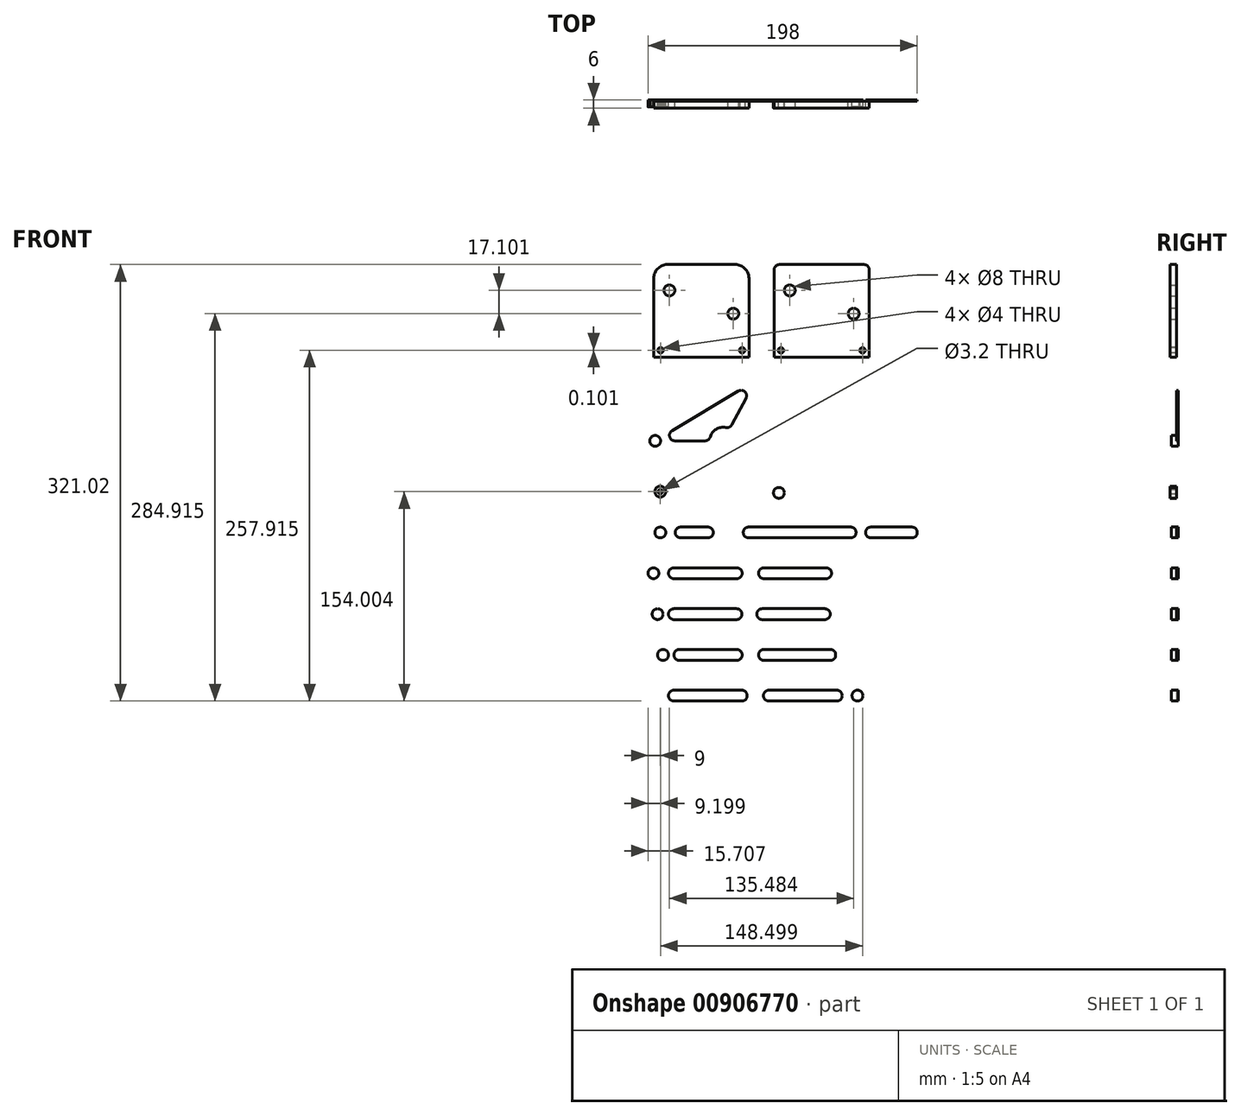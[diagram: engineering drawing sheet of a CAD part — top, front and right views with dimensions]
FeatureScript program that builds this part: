
annotation { "Feature Type Name" : "Feature", "Feature Type Description" : "" }
export const myFeature = defineFeature(function(context is Context, id is Id, definition is map)
    precondition{}
    {
        {
            var Q0;
            Q0=qCreatedBy(makeId("Front.planeOp"),FACE);
            var sketch = newSketch(context, id + "F0", { "sketchPlane" : qUnion([Q0])});
            skCircle(sketch, "E0", {"center": v(-102.5, -60.26) * mm, "radius": 4 * mm});
            skCircle(sketch, "E1", {"center": v(39.5, -60.26) * mm, "radius": 4 * mm});
            skCircle(sketch, "E2", {"center": v(-101.24, 37.12) * mm, "radius": 4 * mm});
            skCircle(sketch, "E3", {"center": v(-51.24, 37.12) * mm, "radius": 4 * mm});
            skCircle(sketch, "E4", {"center": v(-97.5, -30.26) * mm, "radius": 4 * mm});
            skCircle(sketch, "E5", {"center": v(47.5, -150.26) * mm, "radius": 4 * mm});
            skCircle(sketch, "E6", {"center": v(-102.5, -150.26) * mm, "radius": 4 * mm});
            skCircle(sketch, "E7", {"center": v(-97.5, -0.26) * mm, "radius": 4 * mm});
            skCircle(sketch, "E8", {"center": v(-47.5, -0.26) * mm, "radius": 4 * mm});
            skArc(sketch, "E9", {"start": v(-102.5, -142.76) * mm, "mid": v(-110, -150.26) * mm, "end": v(-102.5, -157.76) * mm});
            skArc(sketch, "E10", {"start": v(47.5, -157.76) * mm, "mid": v(55, -150.26) * mm, "end": v(47.5, -142.76) * mm});
            skLineSegment(sketch, "E11", {"start": v(47.5, -142.76) * mm, "end": v(-102.5, -142.76) * mm});
            skLineSegment(sketch, "E12", {"start": v(47.5, -157.76) * mm, "end": v(-102.5, -157.76) * mm});
            skArc(sketch, "E13", {"start": v(-87.5, -146.26) * mm, "mid": v(-91.5, -150.26) * mm, "end": v(-87.5, -154.26) * mm});
            skArc(sketch, "E14", {"start": v(-37.62, -154.26) * mm, "mid": v(-33.62, -150.26) * mm, "end": v(-37.62, -146.26) * mm});
            skLineSegment(sketch, "E15", {"start": v(-87.5, -146.26) * mm, "end": v(-37.62, -146.26) * mm});
            skLineSegment(sketch, "E16", {"start": v(-87.5, -154.26) * mm, "end": v(-37.62, -154.26) * mm});
            skLineSegment(sketch, "E17", {"start": v(32.27, -146.26) * mm, "end": v(-17.62, -146.26) * mm});
            skLineSegment(sketch, "E18", {"start": v(32.27, -154.26) * mm, "end": v(-17.62, -154.26) * mm});
            skArc(sketch, "E19", {"start": v(32.27, -154.26) * mm, "mid": v(36.27, -150.26) * mm, "end": v(32.27, -146.26) * mm});
            skArc(sketch, "E20", {"start": v(-17.62, -146.26) * mm, "mid": v(-21.62, -150.26) * mm, "end": v(-17.62, -154.26) * mm});
            skArc(sketch, "E21", {"start": v(-102.5, -52.76) * mm, "mid": v(-110, -60.26) * mm, "end": v(-102.5, -67.76) * mm});
            skArc(sketch, "E22", {"start": v(39.5, -67.76) * mm, "mid": v(47, -60.26) * mm, "end": v(39.5, -52.76) * mm});
            skLineSegment(sketch, "E23", {"start": v(-102.5, -52.76) * mm, "end": v(39.5, -52.76) * mm});
            skLineSegment(sketch, "E24", {"start": v(39.5, -52.76) * mm, "end": v(-8.11, -52.76) * mm});
            skLineSegment(sketch, "E25", {"start": v(-102.5, -67.76) * mm, "end": v(39.5, -67.76) * mm});
            skArc(sketch, "E26", {"start": v(-87.5, -56.26) * mm, "mid": v(-91.5, -60.26) * mm, "end": v(-87.5, -64.26) * mm});
            skArc(sketch, "E27", {"start": v(-41.27, -64.26) * mm, "mid": v(-37.27, -60.26) * mm, "end": v(-41.27, -56.26) * mm});
            skLineSegment(sketch, "E28", {"start": v(-87.5, -56.26) * mm, "end": v(-41.27, -56.26) * mm});
            skLineSegment(sketch, "E29", {"start": v(-87.5, -64.26) * mm, "end": v(-41.27, -64.26) * mm});
            skLineSegment(sketch, "E30", {"start": v(24.5, -56.26) * mm, "end": v(-21.27, -56.26) * mm});
            skLineSegment(sketch, "E31", {"start": v(24.5, -64.26) * mm, "end": v(-21.27, -64.26) * mm});
            skArc(sketch, "E32", {"start": v(-21.27, -56.26) * mm, "mid": v(-25.27, -60.26) * mm, "end": v(-21.27, -64.26) * mm});
            skArc(sketch, "E33", {"start": v(-97.5, 7.24) * mm, "mid": v(-105, -0.26) * mm, "end": v(-97.5, -7.76) * mm});
            skArc(sketch, "E34", {"start": v(-47.5, -7.76) * mm, "mid": v(-40, -0.26) * mm, "end": v(-47.5, 7.24) * mm});
            skLineSegment(sketch, "E35", {"start": v(-97.5, 7.24) * mm, "end": v(-47.5, 7.24) * mm});
            skLineSegment(sketch, "E36", {"start": v(-97.5, -7.76) * mm, "end": v(-47.5, -7.76) * mm});
            skCircle(sketch, "E37", {"center": v(-10.28, -1.13) * mm, "radius": 4 * mm});
            skCircle(sketch, "E38", {"center": v(39.72, -1.13) * mm, "radius": 4 * mm});
            skLineSegment(sketch, "E39", {"start": v(-10.28, 6.37) * mm, "end": v(39.72, 6.37) * mm});
            skLineSegment(sketch, "E40", {"start": v(39.72, -8.63) * mm, "end": v(-10.28, -8.63) * mm});
            skArc(sketch, "E41", {"start": v(-10.28, 6.37) * mm, "mid": v(-17.78, -1.13) * mm, "end": v(-10.28, -8.63) * mm});
            skArc(sketch, "E42", {"start": v(39.72, -8.63) * mm, "mid": v(47.22, -1.13) * mm, "end": v(39.72, 6.37) * mm});
            skArc(sketch, "E43", {"start": v(24.5, -64.26) * mm, "mid": v(28.5, -60.26) * mm, "end": v(24.5, -56.26) * mm});
            skCircle(sketch, "E44", {"center": v(-99.5, -90.32) * mm, "radius": 4 * mm});
            skCircle(sketch, "E45", {"center": v(35.5, -90.32) * mm, "radius": 4 * mm});
            skArc(sketch, "E46", {"start": v(-87.5, -86.32) * mm, "mid": v(-91.5, -90.32) * mm, "end": v(-87.5, -94.32) * mm});
            skArc(sketch, "E47", {"start": v(-41.5, -94.32) * mm, "mid": v(-37.5, -90.32) * mm, "end": v(-41.5, -86.32) * mm});
            skLineSegment(sketch, "E48", {"start": v(-87.5, -86.32) * mm, "end": v(-41.27, -86.32) * mm});
            skLineSegment(sketch, "E49", {"start": v(-87.5, -94.32) * mm, "end": v(-41.27, -94.32) * mm});
            skArc(sketch, "E50", {"start": v(-22.5, -86.32) * mm, "mid": v(-26.5, -90.32) * mm, "end": v(-22.5, -94.32) * mm});
            skLineSegment(sketch, "E51", {"start": v(35.5, -82.82) * mm, "end": v(-8.11, -82.82) * mm});
            skLineSegment(sketch, "E52", {"start": v(-99.5, -97.82) * mm, "end": v(35.5, -97.82) * mm});
            skLineSegment(sketch, "E53", {"start": v(-99.5, -82.82) * mm, "end": v(35.5, -82.82) * mm});
            skArc(sketch, "E54", {"start": v(23.5, -94.32) * mm, "mid": v(27.5, -90.32) * mm, "end": v(23.5, -86.32) * mm});
            skLineSegment(sketch, "E55", {"start": v(24.5, -86.32) * mm, "end": v(-22.5, -86.32) * mm});
            skLineSegment(sketch, "E56", {"start": v(24.5, -94.32) * mm, "end": v(-22.5, -94.32) * mm});
            skCircle(sketch, "E57", {"center": v(-95.5, -120.32) * mm, "radius": 4 * mm});
            skCircle(sketch, "E58", {"center": v(39.5, -120.32) * mm, "radius": 4 * mm});
            skArc(sketch, "E59", {"start": v(39.5, -127.82) * mm, "mid": v(47, -120.32) * mm, "end": v(39.5, -112.82) * mm});
            skArc(sketch, "E60", {"start": v(-83.5, -116.32) * mm, "mid": v(-87.5, -120.32) * mm, "end": v(-83.5, -124.32) * mm});
            skArc(sketch, "E61", {"start": v(-41.27, -124.32) * mm, "mid": v(-37.27, -120.32) * mm, "end": v(-41.27, -116.32) * mm});
            skLineSegment(sketch, "E62", {"start": v(-83.5, -116.32) * mm, "end": v(-39.27, -116.32) * mm});
            skLineSegment(sketch, "E63", {"start": v(-83.5, -124.32) * mm, "end": v(-39.27, -124.32) * mm});
            skArc(sketch, "E64", {"start": v(-21.27, -116.32) * mm, "mid": v(-25.27, -120.32) * mm, "end": v(-21.27, -124.32) * mm});
            skLineSegment(sketch, "E65", {"start": v(39.5, -112.82) * mm, "end": v(-8.11, -112.82) * mm});
            skLineSegment(sketch, "E66", {"start": v(-95.5, -127.82) * mm, "end": v(39.5, -127.82) * mm});
            skLineSegment(sketch, "E67", {"start": v(-95.5, -112.82) * mm, "end": v(39.5, -112.82) * mm});
            skArc(sketch, "E68", {"start": v(27.5, -124.32) * mm, "mid": v(31.5, -120.32) * mm, "end": v(27.5, -116.32) * mm});
            skLineSegment(sketch, "E69", {"start": v(27.5, -116.32) * mm, "end": v(-21.27, -116.32) * mm});
            skLineSegment(sketch, "E70", {"start": v(27.5, -124.32) * mm, "end": v(-21.27, -124.32) * mm});
            skCircle(sketch, "E71", {"center": v(-47.5, -30.26) * mm, "radius": 4 * mm});
            skArc(sketch, "E72", {"start": v(-97.5, -22.76) * mm, "mid": v(-105, -30.26) * mm, "end": v(-97.5, -37.76) * mm});
            skLineSegment(sketch, "E73", {"start": v(-97.5, -22.76) * mm, "end": v(102.5, -22.76) * mm});
            skLineSegment(sketch, "E74", {"start": v(102.5, -37.76) * mm, "end": v(-97.5, -37.76) * mm});
            skArc(sketch, "E75", {"start": v(-82.5, -26.26) * mm, "mid": v(-86.5, -30.26) * mm, "end": v(-82.5, -34.26) * mm});
            skArc(sketch, "E76", {"start": v(-62.5, -34.26) * mm, "mid": v(-58.5, -30.26) * mm, "end": v(-62.5, -26.26) * mm});
            skArc(sketch, "E77", {"start": v(-32.5, -26.26) * mm, "mid": v(-36.5, -30.26) * mm, "end": v(-32.5, -34.26) * mm});
            skArc(sketch, "E78", {"start": v(87.5, -34.26) * mm, "mid": v(91.5, -30.26) * mm, "end": v(87.5, -26.26) * mm});
            skLineSegment(sketch, "E79", {"start": v(-82.5, -26.26) * mm, "end": v(-62.5, -26.26) * mm});
            skLineSegment(sketch, "E80", {"start": v(-62.5, -34.26) * mm, "end": v(-82.5, -34.26) * mm});
            skArc(sketch, "E81", {"start": v(42.5, -34.26) * mm, "mid": v(46.5, -30.26) * mm, "end": v(42.5, -26.26) * mm});
            skArc(sketch, "E82", {"start": v(57.5, -26.26) * mm, "mid": v(53.5, -30.26) * mm, "end": v(57.5, -34.26) * mm});
            skLineSegment(sketch, "E83", {"start": v(-32.5, -26.26) * mm, "end": v(42.5, -26.26) * mm});
            skLineSegment(sketch, "E84", {"start": v(57.5, -26.26) * mm, "end": v(87.5, -26.26) * mm});
            skLineSegment(sketch, "E85", {"start": v(57.5, -34.26) * mm, "end": v(87.5, -34.26) * mm});
            skLineSegment(sketch, "E86", {"start": v(-32.5, -34.26) * mm, "end": v(42.5, -34.26) * mm});
            skCircle(sketch, "E87", {"center": v(102.5, -30.26) * mm, "radius": 4 * mm});
            skArc(sketch, "E88", {"start": v(102.5, -37.76) * mm, "mid": v(110, -30.26) * mm, "end": v(102.5, -22.76) * mm});
            skCircle(sketch, "E89", {"center": v(14.72, -1.07) * mm, "radius": 3.25 * mm});
            skCircle(sketch, "E90", {"center": v(-27.7, 81.17) * mm, "radius": 4 * mm});
            skArc(sketch, "E91", {"start": v(-105.1, 43.55) * mm, "mid": v(-108.47, 35.12) * mm, "end": v(-101.24, 29.62) * mm});
            skArc(sketch, "E92", {"start": v(-51.24, 29.62) * mm, "mid": v(-47.39, 30.68) * mm, "end": v(-44.63, 33.58) * mm});
            skArc(sketch, "E93", {"start": v(-21.09, 77.63) * mm, "mid": v(-22.53, 86.6) * mm, "end": v(-31.56, 87.6) * mm});
            skLineSegment(sketch, "E94", {"start": v(-86.78, 37.12) * mm, "end": v(-64.66, 37.12) * mm});
            skLineSegment(sketch, "E95", {"start": v(-44.92, 48.95) * mm, "end": v(-34.51, 68.43) * mm});
            skLineSegment(sketch, "E96", {"start": v(-40.1, 73.75) * mm, "end": v(-88.84, 44.55) * mm});
            skLineSegment(sketch, "E97", {"start": v(-31.56, 87.6) * mm, "end": v(-105.1, 43.55) * mm});
            skLineSegment(sketch, "E98", {"start": v(-44.63, 33.58) * mm, "end": v(-21.09, 77.63) * mm});
            skLineSegment(sketch, "E99", {"start": v(-101.24, 29.62) * mm, "end": v(-51.24, 29.62) * mm});
            skArc(sketch, "E100", {"start": v(-88.84, 44.55) * mm, "mid": v(-90.64, 40.05) * mm, "end": v(-86.78, 37.12) * mm});
            skArc(sketch, "E101", {"start": v(-34.51, 68.43) * mm, "mid": v(-35.28, 73.21) * mm, "end": v(-40.1, 73.75) * mm});
            skArc(sketch, "E102", {"start": v(-49.25, 46.92) * mm, "mid": v(-56.38, 45.7) * mm, "end": v(-60.83, 39.97) * mm});
            skArc(sketch, "E103", {"start": v(-49.25, 46.92) * mm, "mid": v(-46.75, 47.21) * mm, "end": v(-44.92, 48.95) * mm});
            skArc(sketch, "E104", {"start": v(-64.66, 37.12) * mm, "mid": v(-62.27, 37.9) * mm, "end": v(-60.83, 39.97) * mm});
            skLineSegment(sketch, "E105", {"start": v(-102.3, 98.76) * mm, "end": v(-32.3, 98.76) * mm});
            skLineSegment(sketch, "E106", {"start": v(-102.3, 166.76) * mm, "end": v(-102.3, 98.65) * mm});
            skLineSegment(sketch, "E107", {"start": v(-32.3, 98.65) * mm, "end": v(-32.3, 166.76) * mm});
            skCircle(sketch, "E108", {"center": v(-90.8, 147.76) * mm, "radius": 4 * mm});
            skCircle(sketch, "E109", {"center": v(-43.8, 130.65) * mm, "radius": 4 * mm});
            skLineSegment(sketch, "E110", {"start": v(-13.8, 98.65) * mm, "end": v(56.2, 98.65) * mm});
            skLineSegment(sketch, "E111", {"start": v(-9.8, 166.76) * mm, "end": v(52.2, 166.76) * mm});
            skLineSegment(sketch, "E112", {"start": v(-13.8, 162.76) * mm, "end": v(-13.8, 98.65) * mm});
            skLineSegment(sketch, "E113", {"start": v(56.2, 98.65) * mm, "end": v(56.2, 162.76) * mm});
            skCircle(sketch, "E114", {"center": v(-2.3, 147.76) * mm, "radius": 4 * mm});
            skCircle(sketch, "E115", {"center": v(44.7, 130.65) * mm, "radius": 4 * mm});
            skArc(sketch, "E116", {"start": v(56.2, 162.76) * mm, "mid": v(55.03, 165.58) * mm, "end": v(52.2, 166.76) * mm});
            skArc(sketch, "E117", {"start": v(-9.8, 166.76) * mm, "mid": v(-12.63, 165.58) * mm, "end": v(-13.8, 162.76) * mm});
            skCircle(sketch, "E118", {"center": v(-97.5, -0.26) * mm, "radius": 1.6 * mm});
            skCircle(sketch, "E119", {"center": v(-47.5, -0.26) * mm, "radius": 1.6 * mm});
            skArc(sketch, "E120", {"start": v(-95.5, -112.82) * mm, "mid": v(-103, -120.32) * mm, "end": v(-95.5, -127.82) * mm});
            skArc(sketch, "E121", {"start": v(35.5, -97.82) * mm, "mid": v(43, -90.32) * mm, "end": v(35.5, -82.82) * mm});
            skArc(sketch, "E122", {"start": v(-99.5, -82.82) * mm, "mid": v(-107, -90.32) * mm, "end": v(-99.5, -97.82) * mm});
            skLineSegment(sketch, "E123.0", {"start": v(-102.3, 166.76) * mm, "end": v(-32.3, 166.76) * mm});
            skSolve(sketch);
        }
        {
            var Q0;
            Q0=makeQuery(id+"F0.imprint","IMPRINT",FACE,{"disambiguationData":[TD([[makeQuery(id+"F0.imprint","IMPRINT",EDGE,{"derivedFrom":sQuery(id+"F0.wireOp",EDGE,"E105")}),1.0]])]});
            extrude(context, id + "F1", {"entities" : qUnion([Q0]), "depth" : 5 * mm, "offsetDistance" : 25 * mm});
        }
        {
            var Q0;
            Q0=makeQuery(id+"F0.imprint","IMPRINT",FACE,{"disambiguationData":[TD([[makeQuery(id+"F0.imprint","IMPRINT",EDGE,{"derivedFrom":sQuery(id+"F0.wireOp",EDGE,"E2")}),1.0]])]});
            extrude(context, id + "F2", {"entities" : qUnion([Q0]), "depth" : 4 * mm, "offsetDistance" : 25 * mm});
        }
        {
            var Q0;
            Q0=makeQuery(id+"F0.imprint","IMPRINT",FACE,{"disambiguationData":[TD([[makeQuery(id+"F0.imprint","IMPRINT",EDGE,{"derivedFrom":sQuery(id+"F0.wireOp",EDGE,"E94")}),1.0]])]});
            var Q1;
            Q1=makeQuery(id+"F0.imprint","IMPRINT",FACE,{"disambiguationData":[TD([[makeQuery(id+"F0.imprint","IMPRINT",EDGE,{"derivedFrom":sQuery(id+"F0.wireOp",EDGE,"E2")}),1.0]])]});
            extrude(context, id + "F3", {"entities" : qUnion([Q0, Q1]), "operationType" : NewBodyOperationType.ADD, "oppositeDirection" : true, "depth" : 1 * mm, "offsetDistance" : 25 * mm});
        }
        {
            var Q0;
            Q0=makeQuery(id+"F0.imprint","IMPRINT",FACE,{"disambiguationData":[TD([[makeQuery(id+"F0.imprint","IMPRINT",EDGE,{"derivedFrom":sQuery(id+"F0.wireOp",EDGE,"E4")}),1.0]])]});
            extrude(context, id + "F4", {"entities" : qUnion([Q0]), "depth" : 4 * mm, "offsetDistance" : 25 * mm});
        }
        {
            var Q0;
            Q0=makeQuery(id+"F4.opExtrude","CAP_FACE",FACE,{"disambiguationData":[OSD([sQuery(id+"F0.wireOp",EDGE,"E4"),sQuery(id+"F0.wireOp",EDGE,"E71"),sQuery(id+"F0.wireOp",EDGE,"E72"),sQuery(id+"F0.wireOp",EDGE,"E73"),sQuery(id+"F0.wireOp",EDGE,"E74"),sQuery(id+"F0.wireOp",EDGE,"E75"),sQuery(id+"F0.wireOp",EDGE,"E76"),sQuery(id+"F0.wireOp",EDGE,"E77"),sQuery(id+"F0.wireOp",EDGE,"E78"),sQuery(id+"F0.wireOp",EDGE,"E79"),sQuery(id+"F0.wireOp",EDGE,"E80"),sQuery(id+"F0.wireOp",EDGE,"E81"),sQuery(id+"F0.wireOp",EDGE,"E82"),sQuery(id+"F0.wireOp",EDGE,"E83"),sQuery(id+"F0.wireOp",EDGE,"E84"),sQuery(id+"F0.wireOp",EDGE,"E85"),sQuery(id+"F0.wireOp",EDGE,"E86"),sQuery(id+"F0.wireOp",EDGE,"E87"),sQuery(id+"F0.wireOp",EDGE,"E88")])],"isStart":false});
            var Q1;
            Q1=makeQuery(id+"F0.imprint","IMPRINT",FACE,{"disambiguationData":[TD([[makeQuery(id+"F0.imprint","IMPRINT",EDGE,{"derivedFrom":sQuery(id+"F0.wireOp",EDGE,"E75")}),1.0]])]});
            var Q2;
            Q2=makeQuery(id+"F0.imprint","IMPRINT",FACE,{"disambiguationData":[TD([[makeQuery(id+"F0.imprint","IMPRINT",EDGE,{"derivedFrom":sQuery(id+"F0.wireOp",EDGE,"E77")}),1.0]])]});
            var Q3;
            Q3=makeQuery(id+"F0.imprint","IMPRINT",FACE,{"disambiguationData":[TD([[makeQuery(id+"F0.imprint","IMPRINT",EDGE,{"derivedFrom":sQuery(id+"F0.wireOp",EDGE,"E78")}),1.0]])]});
            extrude(context, id + "F5", {"entities" : qUnion([Q0, Q1, Q2, Q3]), "operationType" : NewBodyOperationType.ADD, "oppositeDirection" : true, "depth" : 1 * mm, "offsetDistance" : 25 * mm});
        }
        {
            var Q0;
            Q0=makeQuery(id+"F0.imprint","IMPRINT",FACE,{"disambiguationData":[TD([[makeQuery(id+"F0.imprint","IMPRINT",EDGE,{"derivedFrom":sQuery(id+"F0.wireOp",EDGE,"E4")}),1.0]])]});
            var Q1;
            Q1=makeQuery(id+"F0.imprint","IMPRINT",FACE,{"disambiguationData":[TD([[makeQuery(id+"F0.imprint","IMPRINT",EDGE,{"derivedFrom":sQuery(id+"F0.wireOp",EDGE,"E87")}),-1.0]])]});
            var Q2;
            Q2=makeQuery(id+"F0.imprint","IMPRINT",FACE,{"disambiguationData":[TD([[makeQuery(id+"F0.imprint","IMPRINT",EDGE,{"derivedFrom":sQuery(id+"F0.wireOp",EDGE,"E78")}),1.0]])]});
            var Q3;
            Q3=makeQuery(id+"F0.imprint","IMPRINT",FACE,{"disambiguationData":[TD([[makeQuery(id+"F0.imprint","IMPRINT",EDGE,{"derivedFrom":sQuery(id+"F0.wireOp",EDGE,"E77")}),1.0]])]});
            var Q4;
            Q4=makeQuery(id+"F0.imprint","IMPRINT",FACE,{"disambiguationData":[TD([[makeQuery(id+"F0.imprint","IMPRINT",EDGE,{"derivedFrom":sQuery(id+"F0.wireOp",EDGE,"E71")}),-1.0]])]});
            var Q5;
            Q5=makeQuery(id+"F0.imprint","IMPRINT",FACE,{"disambiguationData":[TD([[makeQuery(id+"F0.imprint","IMPRINT",EDGE,{"derivedFrom":sQuery(id+"F0.wireOp",EDGE,"E75")}),1.0]])]});
            var Q6;
            Q6=makeQuery(id+"F0.imprint","IMPRINT",FACE,{"disambiguationData":[TD([[makeQuery(id+"F0.imprint","IMPRINT",EDGE,{"derivedFrom":sQuery(id+"F0.wireOp",EDGE,"E4")}),-1.0]])]});
            extrude(context, id + "F6", {"entities" : qUnion([Q0, Q1, Q2, Q3, Q4, Q5, Q6]), "operationType" : NewBodyOperationType.ADD, "oppositeDirection" : true, "depth" : 1 * mm, "offsetDistance" : 25 * mm});
        }
        {
            var Q0;
            Q0=makeQuery(id+"F0.imprint","IMPRINT",FACE,{"disambiguationData":[TD([[makeQuery(id+"F0.imprint","IMPRINT",EDGE,{"derivedFrom":sQuery(id+"F0.wireOp",EDGE,"E0")}),1.0]])]});
            extrude(context, id + "F7", {"entities" : qUnion([Q0]), "depth" : 4 * mm, "offsetDistance" : 25 * mm});
        }
        {
            var Q0;
            Q0=makeQuery(id+"F0.imprint","IMPRINT",FACE,{"disambiguationData":[TD([[makeQuery(id+"F0.imprint","IMPRINT",EDGE,{"derivedFrom":sQuery(id+"F0.wireOp",EDGE,"E0")}),1.0]])]});
            var Q1;
            Q1=makeQuery(id+"F0.imprint","IMPRINT",FACE,{"disambiguationData":[TD([[makeQuery(id+"F0.imprint","IMPRINT",EDGE,{"derivedFrom":sQuery(id+"F0.wireOp",EDGE,"E1")}),-1.0]])]});
            var Q2;
            Q2=makeQuery(id+"F0.imprint","IMPRINT",FACE,{"disambiguationData":[TD([[makeQuery(id+"F0.imprint","IMPRINT",EDGE,{"derivedFrom":sQuery(id+"F0.wireOp",EDGE,"E30")}),1.0]])]});
            var Q3;
            Q3=makeQuery(id+"F0.imprint","IMPRINT",FACE,{"disambiguationData":[TD([[makeQuery(id+"F0.imprint","IMPRINT",EDGE,{"derivedFrom":sQuery(id+"F0.wireOp",EDGE,"E26")}),1.0]])]});
            var Q4;
            Q4=makeQuery(id+"F0.imprint","IMPRINT",FACE,{"disambiguationData":[TD([[makeQuery(id+"F0.imprint","IMPRINT",EDGE,{"derivedFrom":sQuery(id+"F0.wireOp",EDGE,"E0")}),-1.0]])]});
            extrude(context, id + "F8", {"entities" : qUnion([Q0, Q1, Q2, Q3, Q4]), "operationType" : NewBodyOperationType.ADD, "oppositeDirection" : true, "depth" : 1 * mm, "offsetDistance" : 25 * mm});
        }
        {
            var Q0;
            Q0=makeQuery(id+"F0.imprint","IMPRINT",FACE,{"disambiguationData":[TD([[makeQuery(id+"F0.imprint","IMPRINT",EDGE,{"derivedFrom":sQuery(id+"F0.wireOp",EDGE,"E44")}),1.0]])]});
            extrude(context, id + "F9", {"entities" : qUnion([Q0]), "depth" : 4 * mm, "offsetDistance" : 25 * mm});
        }
        {
            var Q0;
            Q0=makeQuery(id+"F0.imprint","IMPRINT",FACE,{"disambiguationData":[TD([[makeQuery(id+"F0.imprint","IMPRINT",EDGE,{"derivedFrom":sQuery(id+"F0.wireOp",EDGE,"E44")}),1.0]])]});
            var Q1;
            Q1=makeQuery(id+"F0.imprint","IMPRINT",FACE,{"disambiguationData":[TD([[makeQuery(id+"F0.imprint","IMPRINT",EDGE,{"derivedFrom":sQuery(id+"F0.wireOp",EDGE,"E45")}),-1.0]])]});
            var Q2;
            Q2=makeQuery(id+"F0.imprint","IMPRINT",FACE,{"disambiguationData":[TD([[makeQuery(id+"F0.imprint","IMPRINT",EDGE,{"derivedFrom":sQuery(id+"F0.wireOp",EDGE,"E50")}),1.0]])]});
            var Q3;
            Q3=makeQuery(id+"F0.imprint","IMPRINT",FACE,{"disambiguationData":[TD([[makeQuery(id+"F0.imprint","IMPRINT",EDGE,{"derivedFrom":sQuery(id+"F0.wireOp",EDGE,"E46")}),1.0]])]});
            var Q4;
            Q4=makeQuery(id+"F0.imprint","IMPRINT",FACE,{"disambiguationData":[TD([[makeQuery(id+"F0.imprint","IMPRINT",EDGE,{"derivedFrom":sQuery(id+"F0.wireOp",EDGE,"E44")}),-1.0]])]});
            extrude(context, id + "F10", {"entities" : qUnion([Q0, Q1, Q2, Q3, Q4]), "operationType" : NewBodyOperationType.ADD, "oppositeDirection" : true, "depth" : 1 * mm, "offsetDistance" : 25 * mm});
        }
        {
            var Q0;
            Q0=makeQuery(id+"F0.imprint","IMPRINT",FACE,{"disambiguationData":[TD([[makeQuery(id+"F0.imprint","IMPRINT",EDGE,{"derivedFrom":sQuery(id+"F0.wireOp",EDGE,"E57")}),1.0]])]});
            extrude(context, id + "F11", {"entities" : qUnion([Q0]), "depth" : 4 * mm, "offsetDistance" : 25 * mm});
        }
        {
            var Q0;
            Q0=makeQuery(id+"F0.imprint","IMPRINT",FACE,{"disambiguationData":[TD([[makeQuery(id+"F0.imprint","IMPRINT",EDGE,{"derivedFrom":sQuery(id+"F0.wireOp",EDGE,"E57")}),1.0]])]});
            var Q1;
            Q1=makeQuery(id+"F0.imprint","IMPRINT",FACE,{"disambiguationData":[TD([[makeQuery(id+"F0.imprint","IMPRINT",EDGE,{"derivedFrom":sQuery(id+"F0.wireOp",EDGE,"E58")}),-1.0]])]});
            var Q2;
            Q2=makeQuery(id+"F0.imprint","IMPRINT",FACE,{"disambiguationData":[TD([[makeQuery(id+"F0.imprint","IMPRINT",EDGE,{"derivedFrom":sQuery(id+"F0.wireOp",EDGE,"E64")}),1.0]])]});
            var Q3;
            Q3=makeQuery(id+"F0.imprint","IMPRINT",FACE,{"disambiguationData":[TD([[makeQuery(id+"F0.imprint","IMPRINT",EDGE,{"derivedFrom":sQuery(id+"F0.wireOp",EDGE,"E60")}),1.0]])]});
            var Q4;
            Q4=makeQuery(id+"F0.imprint","IMPRINT",FACE,{"disambiguationData":[TD([[makeQuery(id+"F0.imprint","IMPRINT",EDGE,{"derivedFrom":sQuery(id+"F0.wireOp",EDGE,"E57")}),-1.0]])]});
            extrude(context, id + "F12", {"entities" : qUnion([Q0, Q1, Q2, Q3, Q4]), "operationType" : NewBodyOperationType.ADD, "oppositeDirection" : true, "depth" : 1 * mm, "offsetDistance" : 25 * mm});
        }
        {
            var Q0;
            Q0=makeQuery(id+"F0.imprint","IMPRINT",FACE,{"disambiguationData":[TD([[makeQuery(id+"F0.imprint","IMPRINT",EDGE,{"derivedFrom":sQuery(id+"F0.wireOp",EDGE,"E5")}),1.0]])]});
            extrude(context, id + "F13", {"entities" : qUnion([Q0]), "depth" : 4 * mm, "offsetDistance" : 25 * mm});
        }
        {
            var Q0;
            Q0=makeQuery(id+"F0.imprint","IMPRINT",FACE,{"disambiguationData":[TD([[makeQuery(id+"F0.imprint","IMPRINT",EDGE,{"derivedFrom":sQuery(id+"F0.wireOp",EDGE,"E5")}),1.0]])]});
            var Q1;
            Q1=makeQuery(id+"F0.imprint","IMPRINT",FACE,{"disambiguationData":[TD([[makeQuery(id+"F0.imprint","IMPRINT",EDGE,{"derivedFrom":sQuery(id+"F0.wireOp",EDGE,"E5")}),-1.0]])]});
            var Q2;
            Q2=makeQuery(id+"F0.imprint","IMPRINT",FACE,{"disambiguationData":[TD([[makeQuery(id+"F0.imprint","IMPRINT",EDGE,{"derivedFrom":sQuery(id+"F0.wireOp",EDGE,"E17")}),1.0]])]});
            var Q3;
            Q3=makeQuery(id+"F0.imprint","IMPRINT",FACE,{"disambiguationData":[TD([[makeQuery(id+"F0.imprint","IMPRINT",EDGE,{"derivedFrom":sQuery(id+"F0.wireOp",EDGE,"E13")}),1.0]])]});
            var Q4;
            Q4=makeQuery(id+"F0.imprint","IMPRINT",FACE,{"disambiguationData":[TD([[makeQuery(id+"F0.imprint","IMPRINT",EDGE,{"derivedFrom":sQuery(id+"F0.wireOp",EDGE,"E6")}),-1.0]])]});
            extrude(context, id + "F14", {"entities" : qUnion([Q0, Q1, Q2, Q3, Q4]), "operationType" : NewBodyOperationType.ADD, "oppositeDirection" : true, "depth" : 1 * mm, "offsetDistance" : 25 * mm});
        }
        {
            var Q0;
            Q0=makeQuery(id+"F0.imprint","IMPRINT",FACE,{"disambiguationData":[TD([[makeQuery(id+"F0.imprint","IMPRINT",EDGE,{"derivedFrom":sQuery(id+"F0.wireOp",EDGE,"E37")}),1.0]])]});
            extrude(context, id + "F15", {"entities" : qUnion([Q0]), "depth" : 5 * mm, "offsetDistance" : 25 * mm});
        }
        {
            var Q0;
            Q0=makeQuery(id+"F0.imprint","IMPRINT",FACE,{"disambiguationData":[TD([[makeQuery(id+"F0.imprint","IMPRINT",EDGE,{"derivedFrom":sQuery(id+"F0.wireOp",EDGE,"E7")}),1.0]])]});
            extrude(context, id + "F16", {"entities" : qUnion([Q0]), "depth" : 5 * mm, "offsetDistance" : 25 * mm});
        }
        {
            var Q0;
            Q0=makeQuery(id+"F0.imprint","IMPRINT",FACE,{"disambiguationData":[TD([[makeQuery(id+"F0.imprint","IMPRINT",EDGE,{"derivedFrom":sQuery(id+"F0.wireOp",EDGE,"E4")}),-1.0]])]});
            var Q1;
            Q1=makeQuery(id+"F0.imprint","IMPRINT",FACE,{"disambiguationData":[TD([[makeQuery(id+"F0.imprint","IMPRINT",EDGE,{"derivedFrom":sQuery(id+"F0.wireOp",EDGE,"E71")}),-1.0]])]});
            var Q2;
            Q2=makeQuery(id+"F0.imprint","IMPRINT",FACE,{"disambiguationData":[TD([[makeQuery(id+"F0.imprint","IMPRINT",EDGE,{"derivedFrom":sQuery(id+"F0.wireOp",EDGE,"E87")}),-1.0]])]});
            extrude(context, id + "F17", {"entities" : qUnion([Q0, Q1, Q2]), "operationType" : NewBodyOperationType.REMOVE, "oppositeDirection" : true, "depth" : 25 * mm, "offsetDistance" : 25 * mm});
        }
        {
            var Q0;
            Q0=makeQuery(id+"F0.imprint","IMPRINT",FACE,{"disambiguationData":[TD([[makeQuery(id+"F0.imprint","IMPRINT",EDGE,{"derivedFrom":sQuery(id+"F0.wireOp",EDGE,"E0")}),-1.0]])]});
            var Q1;
            Q1=makeQuery(id+"F0.imprint","IMPRINT",FACE,{"disambiguationData":[TD([[makeQuery(id+"F0.imprint","IMPRINT",EDGE,{"derivedFrom":sQuery(id+"F0.wireOp",EDGE,"E1")}),-1.0]])]});
            extrude(context, id + "F18", {"entities" : qUnion([Q0, Q1]), "operationType" : NewBodyOperationType.REMOVE, "oppositeDirection" : true, "depth" : 25 * mm, "offsetDistance" : 25 * mm});
        }
        {
            var Q0;
            Q0=makeQuery(id+"F0.imprint","IMPRINT",FACE,{"disambiguationData":[TD([[makeQuery(id+"F0.imprint","IMPRINT",EDGE,{"derivedFrom":sQuery(id+"F0.wireOp",EDGE,"E44")}),-1.0]])]});
            var Q1;
            Q1=makeQuery(id+"F0.imprint","IMPRINT",FACE,{"disambiguationData":[TD([[makeQuery(id+"F0.imprint","IMPRINT",EDGE,{"derivedFrom":sQuery(id+"F0.wireOp",EDGE,"E45")}),-1.0]])]});
            extrude(context, id + "F19", {"entities" : qUnion([Q0, Q1]), "operationType" : NewBodyOperationType.REMOVE, "oppositeDirection" : true, "depth" : 25 * mm, "offsetDistance" : 25 * mm});
        }
        {
            var Q0;
            Q0=makeQuery(id+"F0.imprint","IMPRINT",FACE,{"disambiguationData":[TD([[makeQuery(id+"F0.imprint","IMPRINT",EDGE,{"derivedFrom":sQuery(id+"F0.wireOp",EDGE,"E57")}),-1.0]])]});
            var Q1;
            Q1=makeQuery(id+"F0.imprint","IMPRINT",FACE,{"disambiguationData":[TD([[makeQuery(id+"F0.imprint","IMPRINT",EDGE,{"derivedFrom":sQuery(id+"F0.wireOp",EDGE,"E58")}),-1.0]])]});
            extrude(context, id + "F20", {"entities" : qUnion([Q0, Q1]), "operationType" : NewBodyOperationType.REMOVE, "oppositeDirection" : true, "depth" : 25 * mm, "offsetDistance" : 25 * mm});
        }
        {
            var Q0;
            Q0=makeQuery(id+"F0.imprint","IMPRINT",FACE,{"disambiguationData":[TD([[makeQuery(id+"F0.imprint","IMPRINT",EDGE,{"derivedFrom":sQuery(id+"F0.wireOp",EDGE,"E6")}),-1.0]])]});
            var Q1;
            Q1=makeQuery(id+"F0.imprint","IMPRINT",FACE,{"disambiguationData":[TD([[makeQuery(id+"F0.imprint","IMPRINT",EDGE,{"derivedFrom":sQuery(id+"F0.wireOp",EDGE,"E5")}),-1.0]])]});
            extrude(context, id + "F21", {"entities" : qUnion([Q0, Q1]), "operationType" : NewBodyOperationType.REMOVE, "oppositeDirection" : true, "depth" : 25 * mm, "offsetDistance" : 25 * mm});
        }
        {
            var Q0;
            Q0=makeQuery(id+"F0.imprint","IMPRINT",FACE,{"disambiguationData":[TD([[makeQuery(id+"F0.imprint","IMPRINT",EDGE,{"derivedFrom":sQuery(id+"F0.wireOp",EDGE,"E110")}),1.0]])]});
            extrude(context, id + "F22", {"entities" : qUnion([Q0]), "depth" : 5 * mm, "offsetDistance" : 25 * mm});
        }
        {
            var Q0;
            Q0=makeQuery(id+"F11.opExtrude","CAP_FACE",FACE,{"disambiguationData":[OSD([sQuery(id+"F0.wireOp",EDGE,"E57"),sQuery(id+"F0.wireOp",EDGE,"E58"),sQuery(id+"F0.wireOp",EDGE,"c3055aba-8b65-4d20-8fe3-df51662e9008"),sQuery(id+"F0.wireOp",EDGE,"E59"),sQuery(id+"F0.wireOp",EDGE,"E60"),sQuery(id+"F0.wireOp",EDGE,"E61"),sQuery(id+"F0.wireOp",EDGE,"E62"),sQuery(id+"F0.wireOp",EDGE,"E63"),sQuery(id+"F0.wireOp",EDGE,"E64"),sQuery(id+"F0.wireOp",EDGE,"E66"),sQuery(id+"F0.wireOp",EDGE,"E67"),sQuery(id+"F0.wireOp",EDGE,"E68"),sQuery(id+"F0.wireOp",EDGE,"E69"),sQuery(id+"F0.wireOp",EDGE,"E70")])],"isStart":false});
            var sketch = newSketch(context, id + "F23", { "sketchPlane" : qUnion([Q0])});
            skCircle(sketch, "E124", {"center": v(-31.5, -120.32) * mm, "radius": 1.5 * mm});
            skSolve(sketch);
        }
        {
            var Q0;
            Q0=makeQuery(id+"F23.imprint","IMPRINT",FACE,{"disambiguationData":[TD([[makeQuery(id+"F23.imprint","IMPRINT",EDGE,{"derivedFrom":sQuery(id+"F23.wireOp",EDGE,"E124")}),1.0]])]});
            var Q1;
            Q1=sQuery(id+"F23.wireOp",EDGE,"E124");
            extrude(context, id + "F24", {"entities" : qUnion([Q0]), "operationType" : NewBodyOperationType.REMOVE, "surfaceEntities" : qUnion([Q1]), "oppositeDirection" : true, "depth" : 25 * mm, "offsetDistance" : 25 * mm});
        }
        {
            var Q0;
            Q0=makeQuery(id+"F9.opExtrude","CAP_FACE",FACE,{"disambiguationData":[OSD([sQuery(id+"F0.wireOp",EDGE,"E44"),sQuery(id+"F0.wireOp",EDGE,"E45"),sQuery(id+"F0.wireOp",EDGE,"e45cf082-d386-4f67-825a-8dd75d7077fc"),sQuery(id+"F0.wireOp",EDGE,"e045fb77-b737-474a-b509-6adc633f4e3b"),sQuery(id+"F0.wireOp",EDGE,"E46"),sQuery(id+"F0.wireOp",EDGE,"E47"),sQuery(id+"F0.wireOp",EDGE,"E48"),sQuery(id+"F0.wireOp",EDGE,"E49"),sQuery(id+"F0.wireOp",EDGE,"E50"),sQuery(id+"F0.wireOp",EDGE,"E52"),sQuery(id+"F0.wireOp",EDGE,"E53"),sQuery(id+"F0.wireOp",EDGE,"E54"),sQuery(id+"F0.wireOp",EDGE,"E55"),sQuery(id+"F0.wireOp",EDGE,"E56")])],"isStart":false});
            var sketch = newSketch(context, id + "F25", { "sketchPlane" : qUnion([Q0])});
            skCircle(sketch, "E125", {"center": v(-32, -90.32) * mm, "radius": 1.5 * mm});
            skSolve(sketch);
        }
        {
            var Q0;
            Q0=makeQuery(id+"F25.imprint","IMPRINT",FACE,{"disambiguationData":[TD([[makeQuery(id+"F25.imprint","IMPRINT",EDGE,{"derivedFrom":sQuery(id+"F25.wireOp",EDGE,"E125")}),1.0]])]});
            extrude(context, id + "F26", {"entities" : qUnion([Q0]), "operationType" : NewBodyOperationType.REMOVE, "oppositeDirection" : true, "depth" : 25 * mm, "offsetDistance" : 25 * mm});
        }
        {
            var Q0;
            Q0=makeQuery(id+"F1.opExtrude","CAP_FACE",FACE,{"disambiguationData":[OSD([sQuery(id+"F0.wireOp",EDGE,"E105"),sQuery(id+"F0.wireOp",EDGE,"dbb09c0b-19ef-4a1c-a7c9-aa244b3878ef"),sQuery(id+"F0.wireOp",EDGE,"E106"),sQuery(id+"F0.wireOp",EDGE,"E107"),sQuery(id+"F0.wireOp",EDGE,"E108"),sQuery(id+"F0.wireOp",EDGE,"E109"),sQuery(id+"F0.wireOp",EDGE,"3b49ab96-93b8-4eb7-a27c-fbe94d797fc8"),sQuery(id+"F0.wireOp",EDGE,"6890914f-84f6-4505-8e57-b99b09f4307f")])],"isStart":false});
            var sketch = newSketch(context, id + "F27", { "sketchPlane" : qUnion([Q0])});
            skCircle(sketch, "E126", {"center": v(-97.3, 103.76) * mm, "radius": 2 * mm});
            skCircle(sketch, "E127", {"center": v(-37.3, 103.76) * mm, "radius": 2 * mm});
            skSolve(sketch);
        }
        {
            var Q0;
            Q0=makeQuery(id+"F27.imprint","IMPRINT",FACE,{"disambiguationData":[TD([[makeQuery(id+"F27.imprint","IMPRINT",EDGE,{"derivedFrom":sQuery(id+"F27.wireOp",EDGE,"E126")}),1.0]])]});
            var Q1;
            Q1=makeQuery(id+"F27.imprint","IMPRINT",FACE,{"disambiguationData":[TD([[makeQuery(id+"F27.imprint","IMPRINT",EDGE,{"derivedFrom":sQuery(id+"F27.wireOp",EDGE,"E127")}),1.0]])]});
            var Q2;
            Q2=sQuery(id+"F27.wireOp",EDGE,"E126");
            extrude(context, id + "F28", {"entities" : qUnion([Q0, Q1]), "operationType" : NewBodyOperationType.REMOVE, "surfaceEntities" : qUnion([Q2]), "oppositeDirection" : true, "depth" : 25 * mm, "offsetDistance" : 25 * mm});
        }
        {
            var Q0;
            Q0=makeQuery(id+"F22.opExtrude","CAP_FACE",FACE,{"disambiguationData":[OSD([sQuery(id+"F0.wireOp",EDGE,"E110"),sQuery(id+"F0.wireOp",EDGE,"E111"),sQuery(id+"F0.wireOp",EDGE,"E112"),sQuery(id+"F0.wireOp",EDGE,"E113"),sQuery(id+"F0.wireOp",EDGE,"E114"),sQuery(id+"F0.wireOp",EDGE,"E115"),sQuery(id+"F0.wireOp",EDGE,"E116"),sQuery(id+"F0.wireOp",EDGE,"E117")])],"isStart":false});
            var sketch = newSketch(context, id + "F29", { "sketchPlane" : qUnion([Q0])});
            skCircle(sketch, "E128", {"center": v(-8.8, 103.65) * mm, "radius": 2 * mm});
            skCircle(sketch, "E129", {"center": v(51.2, 103.65) * mm, "radius": 2 * mm});
            skSolve(sketch);
        }
        {
            var Q0;
            Q0=makeQuery(id+"F29.imprint","IMPRINT",FACE,{"disambiguationData":[TD([[makeQuery(id+"F29.imprint","IMPRINT",EDGE,{"derivedFrom":sQuery(id+"F29.wireOp",EDGE,"E128")}),1.0]])]});
            var Q1;
            Q1=makeQuery(id+"F29.imprint","IMPRINT",FACE,{"disambiguationData":[TD([[makeQuery(id+"F29.imprint","IMPRINT",EDGE,{"derivedFrom":sQuery(id+"F29.wireOp",EDGE,"E129")}),1.0]])]});
            extrude(context, id + "F30", {"entities" : qUnion([Q0, Q1]), "operationType" : NewBodyOperationType.REMOVE, "oppositeDirection" : true, "depth" : 25 * mm, "offsetDistance" : 25 * mm});
        }
        {
            var Q0;
            Q0=makeQuery(id+"F1.opExtrude","SWEPT_EDGE",EDGE,{"disambiguationData":[OSD([sQuery(id+"F0.wireOp",EDGE,"E107"),sQuery(id+"F0.wireOp",EDGE,"E123.0")])]});
            var Q1;
            Q1=makeQuery(id+"F1.opExtrude","SWEPT_EDGE",EDGE,{"disambiguationData":[OSD([sQuery(id+"F0.wireOp",EDGE,"E106"),sQuery(id+"F0.wireOp",EDGE,"E123.0")])]});
            fillet(context, id + "F31", {"entities" : qUnion([Q0, Q1]), "radius" : 10 * mm, "tangentPropagation" : true, "allowEdgeOverflow" : false});
        }
    });
